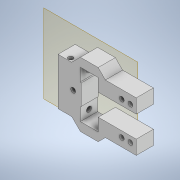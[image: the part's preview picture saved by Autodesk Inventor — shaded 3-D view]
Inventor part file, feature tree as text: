
AUTODESK INVENTOR PART (.ipt)
format: ipt  version: 2022 (Build 260153000, 153)  size: 264,704 bytes
history: native  units: mm
features: reference x9, other x5, sketch x4, extrude x3, projected_geometry x2, plane x1, hole x1, mirror x1
ambient origin geometry x8: Origin, YZ Plane, XZ Plane, XY Plane, X Axis, Y Axis, Z Axis, Center Point
bodies: Volumenkörper1 (feature_tree)
feature tree (26):
  plane  "Arbeitsebene1"
  extrude  "Extrusion1"  Depth=5.0mm
  hole  "Bohrung1"  [1 undecoded]
  extrude  "Extrusion2"  Depth=3.5mm
  mirror  "Spiegeln2"
  extrude  "Extrusion3"  Depth=3.0mm
  sketch  "Skizze1"  dims[d0=0.2mm d2=5.0mm]
  reference  "Referenz1"
  reference  "Referenz2"
  reference  "Referenz3"
  reference  "Referenz4"
  reference  "Referenz5"
  sketch  "Skizze2"  dims[d4=13.0mm d5=2.8mm]
  reference  "Referenz6"
  projected_geometry  "Projizierte Kontur1"
  reference  "Referenz7"
  reference  "Referenz8"
  reference  "Referenz9"
  sketch  "Skizze3"  dims[d7=0.5mm d8=3.5mm]
  sketch  "Skizze4"  dims[d9=10.0mm d10=0.0mm d11=3.0mm d12=3.0mm d13=6.0mm d14=6.0mm d15=4.0mm d16=90.0deg d17=20.0mm d18=20.594885mm d19=0.3mm d20=0.5mm d21=135.0deg d22=2.8mm d23=10.0mm d24=0.0mm d25=7.0mm d26=5.0mm d27=0.0mm d28=8.826939mm]
  projected_geometry  "Projizierte Kontur2"
  other  "Assembly_Cube_Z_Focus_MGN_NEMA_belt_pushing_v3.iam"
  other  "00_MGN12H, LINEAR GUIDE BLOCK:1"
  other  "30_Cube_Z_Focus_MGN_NEMA_base_belt_pushing_v3:1"
  other  "30_Cube_Z_Focus_MGN_NEMA_adapter_RMS:1"
  other  "Baugruppe5"
note: 1 required parameter value undecoded (feature->parameter linkage not recoverable at this tier; creation-order binding heuristic only, values carry confidence <= 0.55)
